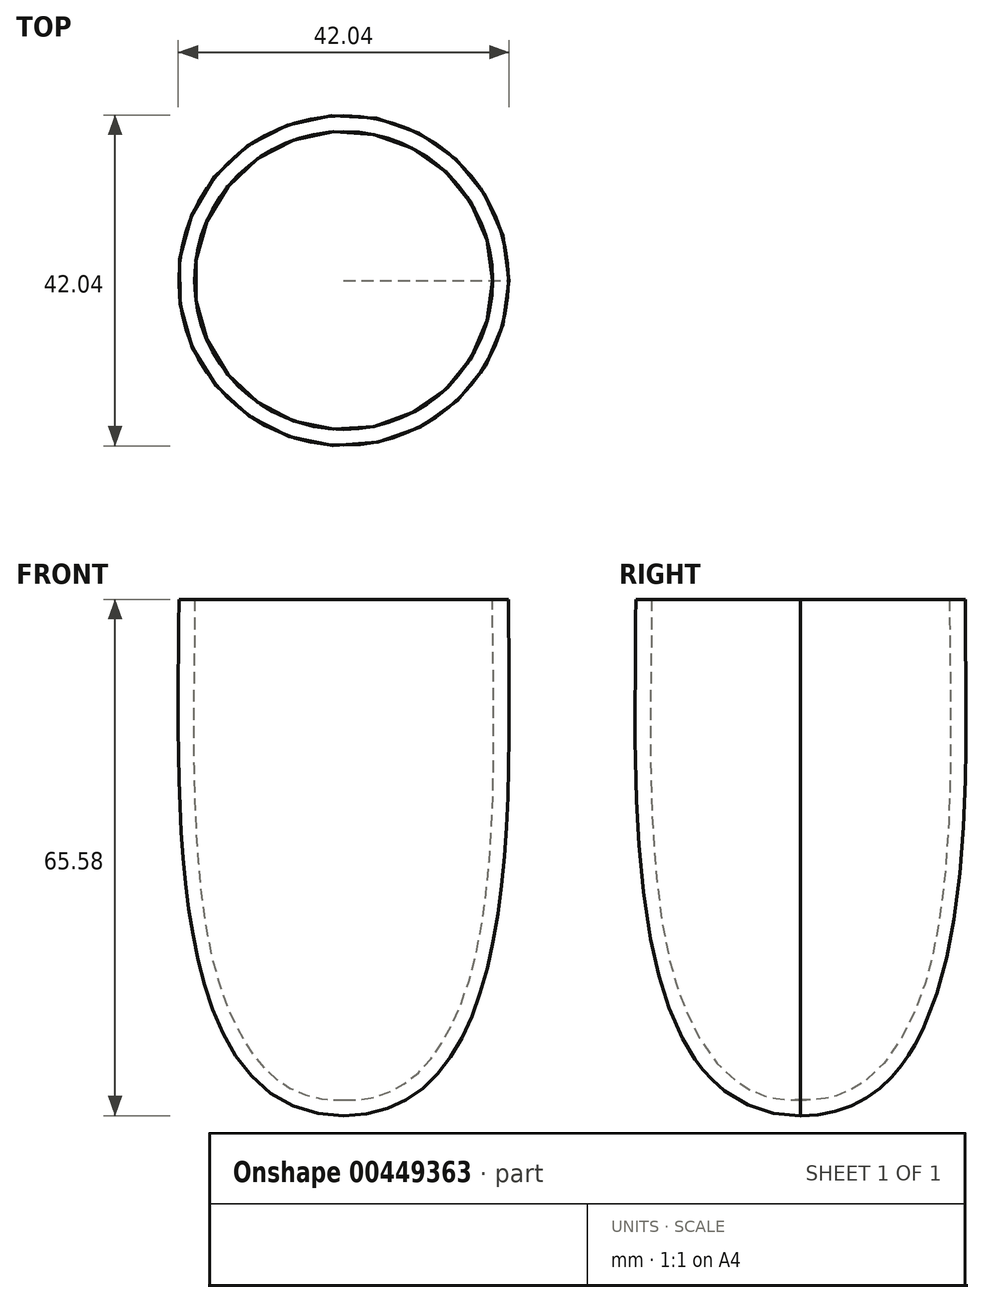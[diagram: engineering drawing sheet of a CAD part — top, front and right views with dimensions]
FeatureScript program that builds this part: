
annotation { "Feature Type Name" : "Feature", "Feature Type Description" : "" }
export const myFeature = defineFeature(function(context is Context, id is Id, definition is map)
    precondition{}
    {
        {
            var Q0;
            Q0=qCreatedBy(makeId("Front.planeOp"),FACE);
            var sketch = newSketch(context, id + "F0", { "sketchPlane" : qUnion([Q0])});
            skLineSegment(sketch, "E0", {"start": v(0, 0) * mm, "end": v(-8.35, 0) * mm, "construction": true});
            skFitSpline(sketch, "E1", {"points": [v(0, 0) * mm, v(20.93, 65.58) * mm], "startDerivative": vector(70.65, 0) * mm, "endDerivative": vector(0, 71.62) * mm});
            skLineSegment(sketch, "E2", {"start": v(20.93, 65.58) * mm, "end": v(20.93, 72.94) * mm, "construction": true});
            skFitSpline(sketch, "E3.0", {"points": [v(0, 2) * mm, v(1.32, 2) * mm, v(3.74, 2.3) * mm, v(6.78, 3.48) * mm, v(9.38, 5.36) * mm, v(11.64, 7.94) * mm, v(13.55, 11.19) * mm, v(15.66, 16.3) * mm, v(17.5, 23.97) * mm, v(18.65, 34.4) * mm, v(19.04, 45.33) * mm, v(19.01, 56.05) * mm, v(18.93, 62.58) * mm, v(18.93, 65.58) * mm]});
            skLineSegment(sketch, "E4", {"start": v(0, 2) * mm, "end": v(0, 0) * mm});
            skLineSegment(sketch, "E5", {"start": v(18.93, 65.58) * mm, "end": v(20.93, 65.58) * mm});
            skSolve(sketch);
        }
        {
            var Q0;
            Q0=makeQuery(id+"F0.imprint","IMPRINT",FACE,{"disambiguationData":[TD([[makeQuery(id+"F0.imprint","IMPRINT",EDGE,{"derivedFrom":sQuery(id+"F0.wireOp",EDGE,"E1")}),1.0]])]});
            var Q1;
            Q1=sQuery(id+"F0.wireOp",EDGE,"E4");
            revolve(context, id + "F1", {"entities" : qUnion([Q0]), "axis" : qUnion([Q1]), "revolveType" : RevolveType.FULL});
        }
    });
